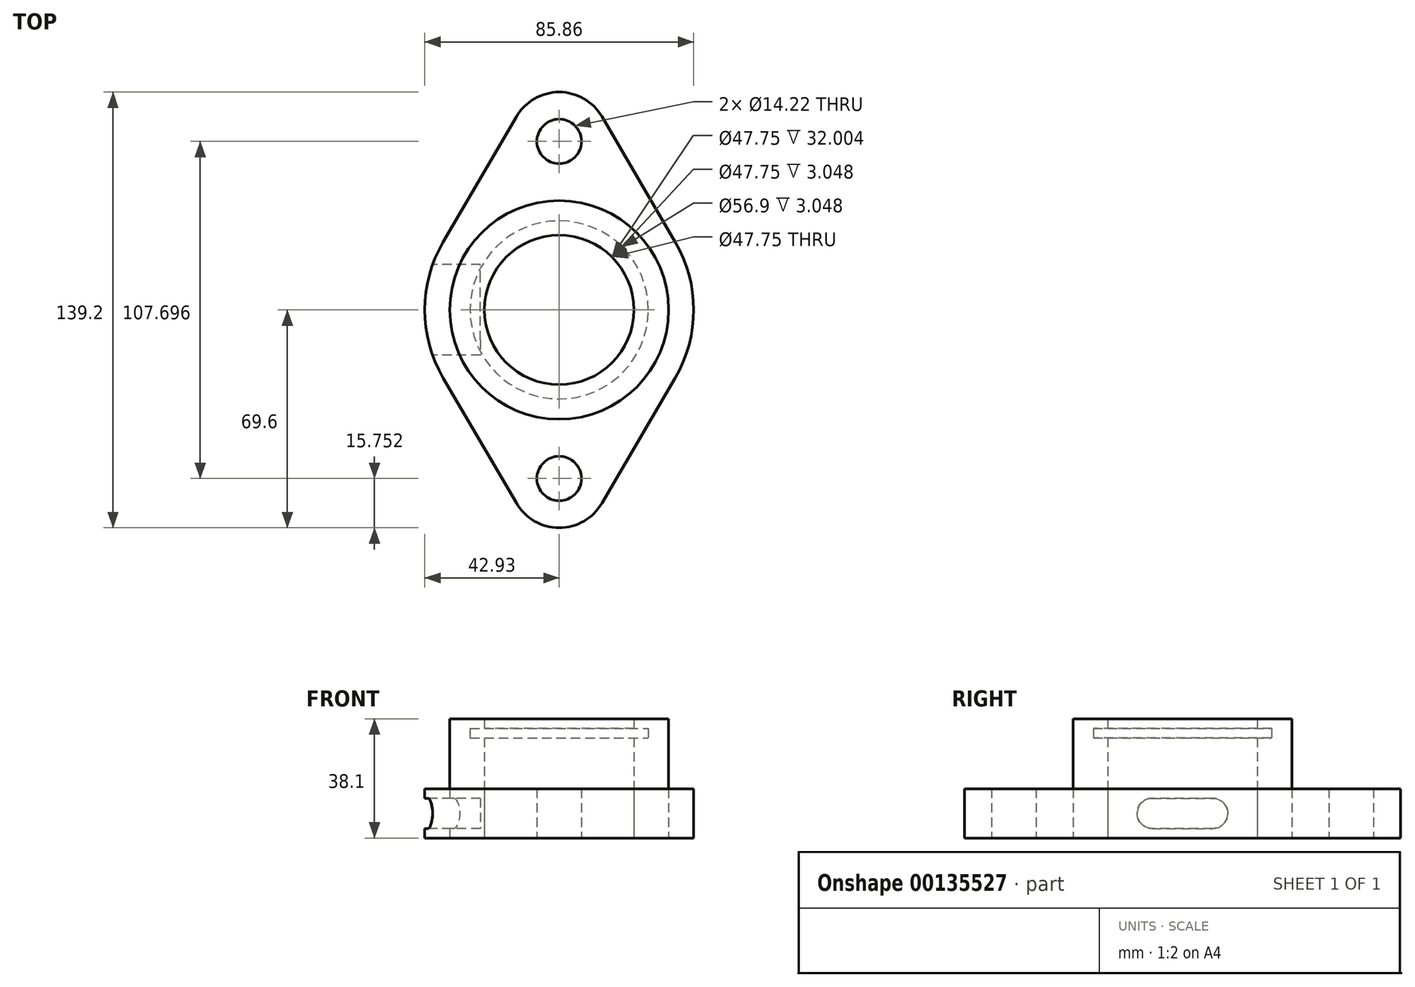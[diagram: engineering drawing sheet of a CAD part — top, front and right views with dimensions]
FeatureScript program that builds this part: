
annotation { "Feature Type Name" : "Feature", "Feature Type Description" : "" }
export const myFeature = defineFeature(function(context is Context, id is Id, definition is map)
    precondition{}
    {
        {
            var Q0;
            Q0=qCreatedBy(makeId("Top.planeOp"),FACE);
            var sketch = newSketch(context, id + "F0", { "sketchPlane" : qUnion([Q0])});
            skArc(sketch, "E0", {"start": v(13.63, 61.74) * mm, "mid": v(0, 69.6) * mm, "end": v(-13.63, 61.74) * mm});
            skArc(sketch, "E1", {"start": v(-13.63, -61.74) * mm, "mid": v(0, -69.6) * mm, "end": v(13.63, -61.74) * mm});
            skCircle(sketch, "E2", {"center": v(0, 53.85) * mm, "radius": 7.11 * mm});
            skCircle(sketch, "E3", {"center": v(0, -53.85) * mm, "radius": 7.11 * mm});
            skLineSegment(sketch, "E4", {"start": v(-13.63, 61.74) * mm, "end": v(-37.06, 21.67) * mm});
            skLineSegment(sketch, "E5", {"start": v(13.63, -61.74) * mm, "end": v(37.06, -21.67) * mm});
            skLineSegment(sketch, "E6", {"start": v(-13.63, -61.74) * mm, "end": v(-37.06, -21.67) * mm});
            skCircle(sketch, "E7", {"center": v(0, 0) * mm, "radius": 34.93 * mm});
            skArc(sketch, "E8", {"start": v(37, 21.77) * mm, "mid": v(42.93, 0.06) * mm, "end": v(37.06, -21.67) * mm});
            skCircle(sketch, "E9", {"center": v(0, 0) * mm, "radius": 23.88 * mm});
            skCircle(sketch, "E10", {"center": v(0, 0) * mm, "radius": 28.58 * mm, "construction": true});
            skCircle(sketch, "E11", {"center": v(0, 0) * mm, "radius": 42.93 * mm});
            skLineSegment(sketch, "E12", {"start": v(13.63, 61.74) * mm, "end": v(37.06, 21.67) * mm});
            skSolve(sketch);
        }
        {
            var Q0;
            Q0 = qSketchRegion(id + "F0", true);
            var Q1;
            Q1=makeQuery(id+"F0.imprint","IMPRINT",FACE,{"disambiguationData":[TD([[makeQuery(id+"F0.imprint","IMPRINT",EDGE,{"derivedFrom":sQuery(id+"F0.wireOp",EDGE,"E7")}),1.0]])]});
            extrude(context, id + "F1", {"entities" : qUnion([Q0, Q1]), "depth" : 15.75 * mm});
        }
        {
            var Q0;
            Q0=makeQuery(id+"F0.imprint","IMPRINT",FACE,{"disambiguationData":[TD([[makeQuery(id+"F0.imprint","IMPRINT",EDGE,{"derivedFrom":sQuery(id+"F0.wireOp",EDGE,"E7")}),1.0]])]});
            extrude(context, id + "F2", {"entities" : qUnion([Q0]), "depth" : 38.1 * mm});
        }
        {
            var Q0;
            Q0=qCreatedBy(makeId("Front.planeOp"),FACE);
            var sketch = newSketch(context, id + "F3", { "sketchPlane" : qUnion([Q0])});
            skLineSegment(sketch, "E13", {"start": v(0, 64) * mm, "end": v(0, 0) * mm, "construction": true});
            skLineSegment(sketch, "E14", {"start": v(0, 32) * mm, "end": v(-28.45, 32) * mm});
            skLineSegment(sketch, "E15", {"start": v(-28.45, 35.05) * mm, "end": v(-28.45, 32) * mm});
            skLineSegment(sketch, "E16", {"start": v(-28.45, 35.05) * mm, "end": v(0, 35.05) * mm});
            skLineSegment(sketch, "E17", {"start": v(0, 32) * mm, "end": v(0, 35.05) * mm});
            skSolve(sketch);
        }
        {
            var Q0;
            Q0=makeQuery(id+"F3.imprint","IMPRINT",FACE,{"disambiguationData":[TD([[makeQuery(id+"F3.imprint","IMPRINT",EDGE,{"derivedFrom":sQuery(id+"F3.wireOp",EDGE,"E14")}),-1.0]])]});
            var Q1;
            Q1=sQuery(id+"F3.wireOp",EDGE,"E13");
            revolve(context, id + "F4", {"operationType" : NewBodyOperationType.REMOVE, "entities" : qUnion([Q0]), "axis" : qUnion([Q1]), "revolveType" : RevolveType.FULL, "oppositeDirection" : true});
        }
        {
            var Q0;
            Q0=qCreatedBy(makeId("Right.planeOp"),FACE);
            cPlane(context, id + "F5", {"entities" : qUnion([Q0]), "cplaneType" : CPlaneType.OFFSET, "offset" : 44.45 * mm, "oppositeDirection" : true, "width" : 152.4 * mm, "height" : 152.4 * mm});
        }
        {
            var Q0;
            Q0=qCreatedBy(id+"F5.planeOp",FACE);
            var sketch = newSketch(context, id + "F6", { "sketchPlane" : qUnion([Q0])});
            skLineSegment(sketch, "E18", {"start": v(-9.65, 12.7) * mm, "end": v(9.65, 12.7) * mm});
            skLineSegment(sketch, "E19", {"start": v(9.65, 3.05) * mm, "end": v(-9.65, 3.05) * mm});
            skArc(sketch, "E20", {"start": v(-9.65, 12.7) * mm, "mid": v(-14.48, 7.87) * mm, "end": v(-9.65, 3.05) * mm});
            skArc(sketch, "E21", {"start": v(9.65, 3.05) * mm, "mid": v(14.48, 7.87) * mm, "end": v(9.65, 12.7) * mm});
            skSolve(sketch);
        }
        {
            var Q0;
            Q0 = qSketchRegion(id + "F6", true);
            var Q1;
            Q1=makeQuery(id+"F4.boolean.opBoolean","COPY",FACE,{"derivedFrom":makeQuery(id+"F4.opRevolve","SWEPT_FACE",FACE,{"disambiguationData":[OSD([sQuery(id+"F3.wireOp",EDGE,"E14")])]})});
            extrude(context, id + "F7", {"entities" : qUnion([Q0]), "operationType" : NewBodyOperationType.REMOVE, "endBoundEntityFace" : qUnion([Q1]), "depth" : 19.3 * mm});
        }
    });
